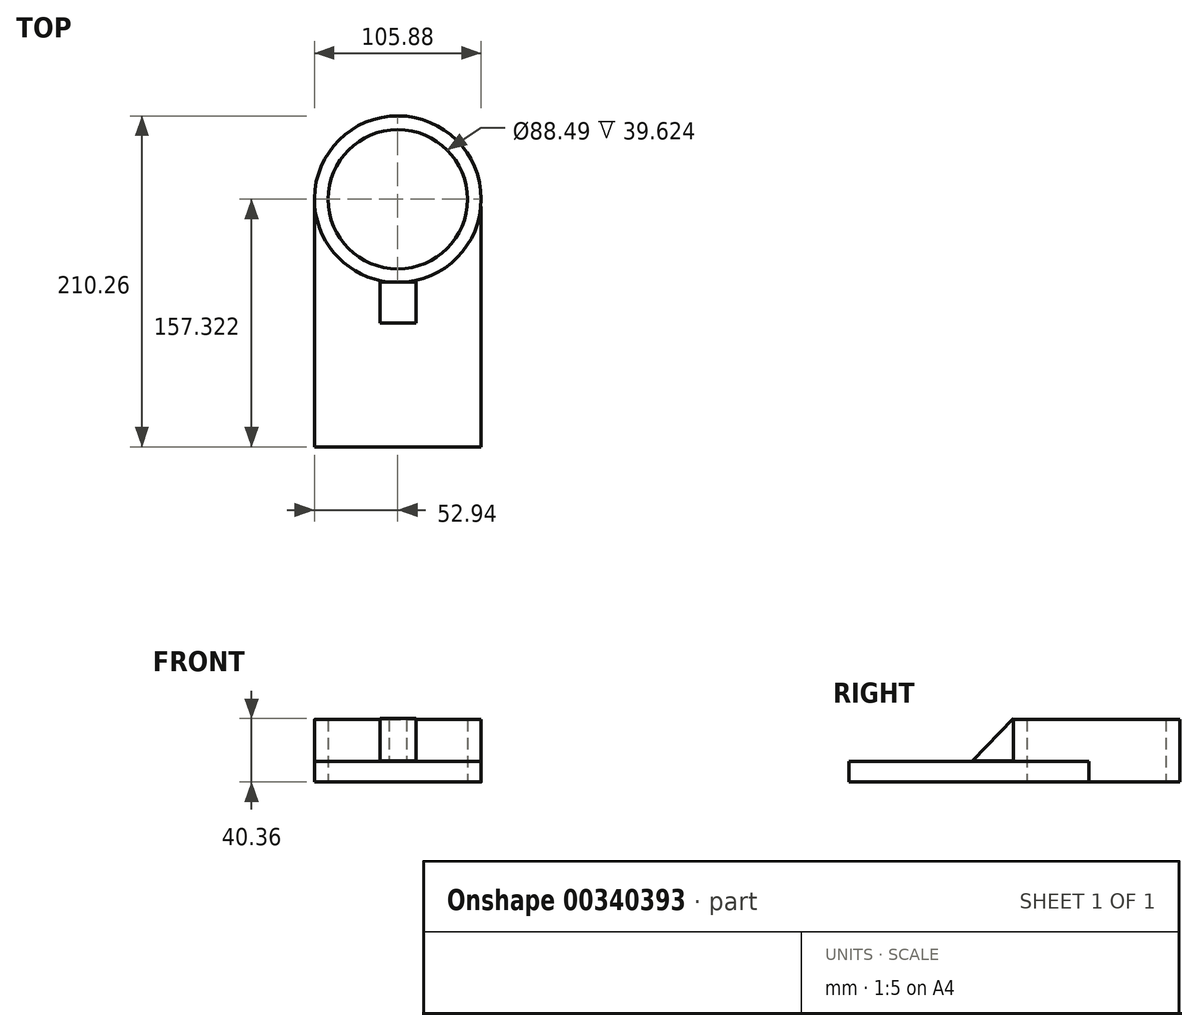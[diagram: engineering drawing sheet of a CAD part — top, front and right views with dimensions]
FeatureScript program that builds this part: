
annotation { "Feature Type Name" : "Feature", "Feature Type Description" : "" }
export const myFeature = defineFeature(function(context is Context, id is Id, definition is map)
    precondition{}
    {
        {
            var Q0;
            Q0=qCreatedBy(makeId("Top.planeOp"),FACE);
            var sketch = newSketch(context, id + "F0", { "sketchPlane" : qUnion([Q0])});
            skLineSegment(sketch, "E0.top", {"start": v(-52.73, -78.66) * mm, "end": v(52.73, -78.66) * mm});
            skLineSegment(sketch, "E0.left", {"start": v(-52.73, 78.66) * mm, "end": v(-52.73, -78.66) * mm});
            skLineSegment(sketch, "E0.right", {"start": v(52.73, 78.66) * mm, "end": v(52.73, -78.66) * mm});
            skPoint(sketch, "E0.middle", {"position": v(0, 0) * mm});
            skCircle(sketch, "E1", {"center": v(0, 78.66) * mm, "radius": 52.94 * mm});
            skCircle(sketch, "E2", {"center": v(0, 78.66) * mm, "radius": 44.25 * mm});
            skSolve(sketch);
        }
        {
            var Q0;
            Q0=makeQuery(id+"F0.imprint","IMPRINT",FACE,{"disambiguationData":[TD([[makeQuery(id+"F0.imprint","IMPRINT",EDGE,{"derivedFrom":sQuery(id+"F0.wireOp",EDGE,"E2")}),-1.0]])]});
            extrude(context, id + "F1", {"entities" : qUnion([Q0]), "depth" : 39.62 * mm});
        }
        {
            var Q0;
            {var subQ0=sQuery(id+"F0.wireOp",EDGE,"E0.top");Q0=makeQuery(id+"F0.imprint","IMPRINT",FACE,{"disambiguationData":[TD([[makeQuery(id+"F0.imprint","IMPRINT",EDGE,{"derivedFrom":subQ0}),1.0]])]});}
            extrude(context, id + "F2", {"entities" : qUnion([Q0]), "operationType" : NewBodyOperationType.ADD, "depth" : 13.2 * mm});
        }
        {
            var Q0;
            Q0=qCreatedBy(makeId("Right.planeOp"),FACE);
            var sketch = newSketch(context, id + "F3", { "sketchPlane" : qUnion([Q0])});
            skLineSegment(sketch, "E3", {"start": v(26.02, 40.36) * mm, "end": v(0, 13.37) * mm});
            skLineSegment(sketch, "E4", {"start": v(0, 13.37) * mm, "end": v(26.02, 13.37) * mm});
            skLineSegment(sketch, "E5", {"start": v(26.02, 13.37) * mm, "end": v(26.02, 40.36) * mm});
            skSolve(sketch);
        }
        {
            var Q0;
            Q0=makeQuery(id+"F3.imprint","IMPRINT",FACE,{"disambiguationData":[TD([[makeQuery(id+"F3.imprint","IMPRINT",EDGE,{"derivedFrom":sQuery(id+"F3.wireOp",EDGE,"E3")}),1.0]])]});
            extrude(context, id + "F4", {"entities" : qUnion([Q0]), "operationType" : NewBodyOperationType.ADD, "endBound" : BoundingType.SYMMETRIC, "depth" : 22.86 * mm});
        }
    });
